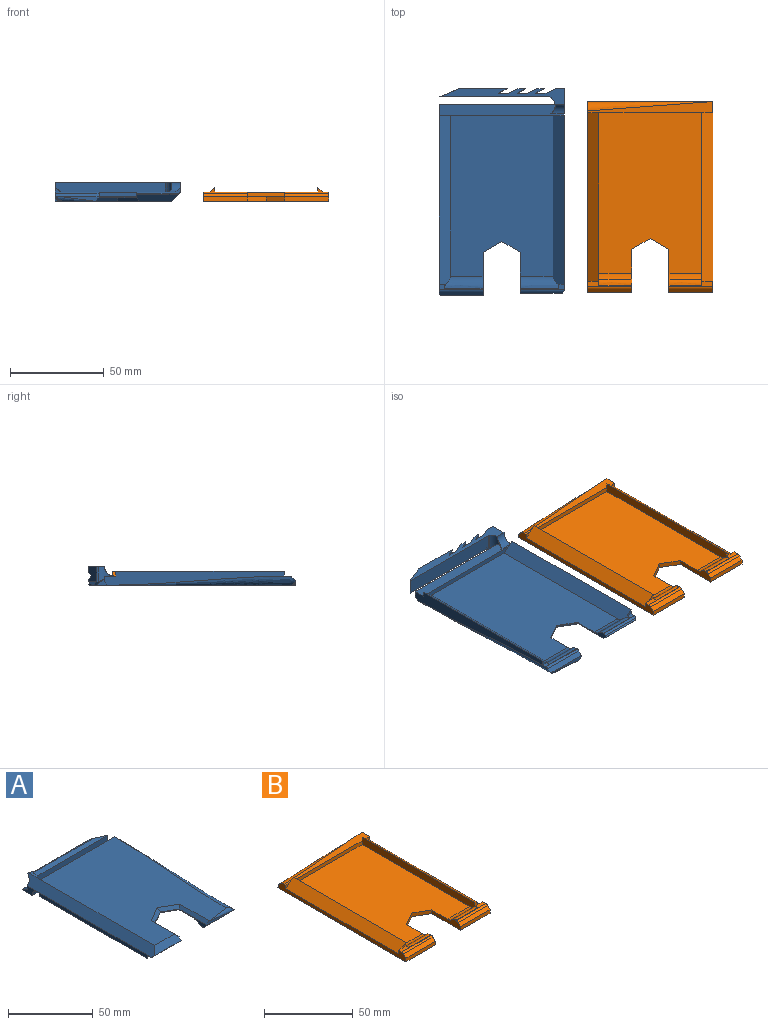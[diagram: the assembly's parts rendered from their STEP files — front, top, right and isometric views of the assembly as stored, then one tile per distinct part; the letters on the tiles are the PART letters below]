
ASSEMBLY  parts=2 mates=1
PART A: 78 faces, bbox 67x117.9x10 mm
  f0: plane 51.83x3.78mm, normal (0,0,1), area 23.2mm2, adj f12,f14,f16,f18,f20,f22,f24,f26
  f1: plane 90x2.5mm, normal (-1,0,0), area 225mm2, adj f41,f44,f48,f62
  f2: plane 3.72x1.44mm, normal (0,1,0), area 4.9mm2, adj f5,f13,f23,f51
  f3: plane 3.84x0.23mm, normal (0,1,0), area 0.4mm2, adj f5,f17,f51
  f4: plane 3.72x0.84mm, normal (0,1,0), area 2.7mm2, adj f5,f11,f19,f51
  f5: plane 67x8.5mm, normal (0,0,-1), area 257.4mm2, adj f2,f3,f4,f6,f7,f9,f11,f13
  f6: plane 13.46x5mm, normal (-1,0,0), area 31.5mm2, adj f5,f50,f51,f62,f75
  f7: plane 11x8mm, normal (0.38,0.93,0), area 87.2mm2, adj f5,f8,f9,f36,f50,f51,f52,f66
  f8: plane 22.52x1.36mm, normal (0,1,0), area 15.3mm2, adj f7,f52,f65
  f9: plane 25.45x3.36mm, normal (0,1,0), area 66mm2, adj f5,f7,f25,f51
  f10: plane 100x62mm, normal (0,0,1), area 5175.6mm2, adj f61,f62,f67,f70,f71,f72,f73,f76
  f11: plane 5.59x2.59mm, normal (0.4,0.92,0), area 10.5mm2, adj f4,f5,f15,f51
  f12: plane 4.04x2.59mm, normal (0.4,0.92,0), area 6.5mm2, adj f0,f16,f52,f69
  f13: plane 4.8x2.92mm, normal (-0.46,-0.89,0), area 11.2mm2, adj f2,f5,f15,f51
  f14: plane 3.89x2.92mm, normal (-0.46,-0.89,0), area 7.2mm2, adj f0,f16,f52,f68
  f15: plane 5.49x2.92mm, normal (0,1,0), area 15.1mm2, adj f5,f11,f13,f51
  f16: plane 5.49x2.92mm, normal (0,1,0), area 15.1mm2, adj f0,f12,f14,f52
  f17: plane 5.59x2.45mm, normal (0.4,0.92,0), area 6.8mm2, adj f3,f5,f21,f51
  f18: plane 5.21x2.29mm, normal (0.4,0.92,0), area 6.6mm2, adj f0,f22,f52,f62
  f19: plane 4.8x2.45mm, normal (-0.46,-0.89,0), area 7.9mm2, adj f4,f5,f21,f51
  f20: plane 3.2x2.32mm, normal (-0.46,-0.89,0), area 4.8mm2, adj f0,f22,f52,f69
  f21: plane 5.49x2.32mm, normal (0,1,0), area 11.8mm2, adj f5,f17,f19,f51
  f22: plane 5.49x2.32mm, normal (0,1,0), area 11.8mm2, adj f0,f18,f20,f52
  f23: plane 5.59x3.2mm, normal (0.4,0.92,0), area 14.2mm2, adj f2,f5,f27,f51
  f24: plane 4.85x3.2mm, normal (0.4,0.92,0), area 9.4mm2, adj f0,f28,f52,f68
  f25: plane 4.8x3.53mm, normal (-0.46,-0.89,0), area 14.4mm2, adj f5,f9,f27,f51
  f26: plane 4.59x3.53mm, normal (-0.46,-0.89,0), area 10mm2, adj f0,f28,f52,f65
  f27: plane 5.49x3.53mm, normal (0,1,0), area 18.5mm2, adj f5,f23,f25,f51
  f28: plane 5.49x3.53mm, normal (0,1,0), area 18.5mm2, adj f0,f24,f26,f52
  f29: plane 62x3mm, normal (0,1,0), area 186mm2, adj f35,f38,f45,f67,f74
  f30: plane 61x2.5mm, normal (0,-1,0), area 145mm2, adj f40,f41,f42,f45
  f31: plane 21.82x3mm, normal (1,0,0), area 23mm2, adj f32,f40,f49,f54,f56,f58,f59,f61
  f32: plane 10x5.77mm, normal (0.5,-0.87,0), area 5.8mm2, adj f31,f33,f40,f71
  f33: plane 10x5.77mm, normal (-0.5,-0.87,0), area 5.8mm2, adj f32,f34,f40,f73
  f34: plane 23.07x3mm, normal (-1,0,0), area 25.9mm2, adj f33,f37,f40,f46,f53,f55,f57,f60
  f35: plane 99.09x7.5mm, normal (1,0,0), area 474.7mm2, adj f29,f42,f43,f45,f46,f47,f67,f77
  f36: plane 59x8mm, normal (0,-1,0), area 472mm2, adj f5,f7,f39,f64
  f37: plane 19.92x2.5mm, normal (0,-1,0), area 25.4mm2, adj f34,f57,f72,f76
  f38: plane 6.4x3.66mm, normal (1,0,0), area 10.1mm2, adj f29,f62,f63,f67
  f39: plane 8x0.82mm, normal (0.55,-0.83,0), area 7.9mm2, adj f5,f36,f63,f74
  f40: plane 85.67x55mm, normal (0,0,-1), area 4399.3mm2, adj f30,f31,f32,f33,f34,f41,f42,f53
  f41: plane 92.28x6mm, normal (0.64,0,-0.77), area 698.9mm2, adj f1,f30,f40,f44,f48,f49,f54,f56
  f42: plane 92.28x6mm, normal (-0.64,0,-0.77), area 698.9mm2, adj f30,f35,f40,f43,f46,f47,f53,f55
  f43: plane 3x2.5mm, normal (0,1,0), area 3.7mm2, adj f35,f42,f45
  f44: plane 3x2.5mm, normal (0,1,0), area 3.7mm2, adj f1,f41,f45
  f45: plane 67x6mm, normal (0,0,-1), area 374.2mm2, adj f29,f30,f35,f43,f44,f62,f74,f75
  f46: plane 23.5x2.67mm, normal (0,0,-1), area 16mm2, adj f34,f35,f42,f47,f55,f60
  f47: plane 3x2.5mm, normal (0,-1,0), area 3.7mm2, adj f35,f42,f46
  f48: plane 3x2.5mm, normal (0,-1,0), area 3.8mm2, adj f1,f41,f49
  f49: plane 23.5x2.67mm, normal (0,0,-1), area 16mm2, adj f31,f41,f48,f56,f59,f62
  f50: plane 59.07x4.95mm, normal (-0.05,1,0), area 188.5mm2, adj f6,f7,f51,f52,f62
  f51: plane 59.07x4.35mm, normal (-0.05,0.5,0.86), area 139.3mm2, adj f2,f3,f4,f5,f6,f7,f9,f11
  f52: plane 56.63x4.23mm, normal (-0.05,0.5,-0.86), area 116.4mm2, adj f7,f8,f12,f14,f16,f18,f20,f22
  f53: cylinder r=5mm len=19mm, axis (-1,0,0), area 65.1mm2, adj f34,f40,f42,f55
  f54: cylinder r=5mm len=19mm, axis (-1,0,0), area 65.1mm2, adj f31,f40,f41,f56
  f55: bspline ~22.55x3.31mm, area 72.4mm2, adj f34,f42,f46,f53
  f56: bspline ~22.55x3.31mm, area 72.4mm2, adj f31,f41,f49,f54
  f57: plane 23.51x1.96mm, normal (0,-0.71,-0.71), area 62.8mm2, adj f34,f37,f60,f76,f77
  f58: plane 22.91x0.66mm, normal (0,-0.71,-0.71), area 21.2mm2, adj f31,f59,f61,f62
  f59: cylinder r=2mm len=23.5mm, axis (1,0,0), area 36.6mm2, adj f31,f49,f58,f62
  f60: cylinder r=2mm len=23.5mm, axis (1,0,0), area 36.9mm2, adj f34,f46,f57,f77
  f61: plane 22.25x3.75mm, normal (0,-0.71,0.71), area 105.2mm2, adj f10,f31,f58,f62,f70
  f62: plane 109.09x5mm, normal (-0.71,0,0.71), area 739.6mm2, adj f0,f1,f6,f10,f18,f38,f45,f49
  f63: plane 6x3.66mm, normal (0.39,-0.59,0.71), area 10.6mm2, adj f0,f38,f39,f64,f74
  f64: plane 59.61x2mm, normal (0,-0.71,0.71), area 153.3mm2, adj f0,f36,f63,f66
  f65: plane 25.24x2mm, normal (0,0.71,0.71), area 65.7mm2, adj f0,f8,f26,f52,f66
  f66: plane 11.39x4.5mm, normal (0.27,0.65,0.71), area 18.7mm2, adj f0,f7,f64,f65
  f67: plane 62x2mm, normal (0,0.71,0.71), area 175.4mm2, adj f10,f29,f35,f38
  f68: plane 7.37x1.68mm, normal (0,0.71,0.71), area 9.3mm2, adj f0,f14,f24,f52
  f69: plane 6.68x1.32mm, normal (0,0.71,0.71), area 7.4mm2, adj f0,f12,f20,f52
  f70: plane 21.23x2mm, normal (0.71,0,0.71), area 55.6mm2, adj f10,f31,f61,f71
  f71: plane 12x8.08mm, normal (0.35,-0.61,0.71), area 35.9mm2, adj f10,f32,f70,f73
  f72: plane 24.23x2mm, normal (-0.71,0,0.71), area 66.9mm2, adj f10,f34,f37,f73
  f73: plane 12x8.08mm, normal (-0.35,-0.61,0.71), area 35.9mm2, adj f10,f33,f71,f72
  f74: cylinder r=5mm len=8.45mm, axis (0,0,1), area 36.7mm2, adj f5,f29,f39,f45,f63,f75
  f75: cylinder r=5mm len=7.38mm, axis (-1,0,0), area 42.1mm2, adj f5,f6,f45,f74
  f76: bspline ~21.5x3mm, area 39.4mm2, adj f10,f37,f57,f77
  f77: bspline ~107.4x5mm, area 397.4mm2, adj f10,f35,f57,f60,f76
PART B: 36 faces, bbox 73.7x102x8 mm
  f0: plane 67x6mm, normal (0,0,1), area 234.5mm2, adj f1,f2,f3,f5,f20,f25,f26,f35
  f1: plane 102x5mm, normal (1,0,0), area 281.8mm2, adj f0,f11,f12,f13,f15,f18,f20,f21
  f2: plane 3x2.5mm, normal (0,-1,0), area 3.7mm2, adj f0,f5,f19
  f3: plane 55x2.5mm, normal (0,-1,0), area 137.5mm2, adj f0,f14,f16,f17
  f4: plane 3x2.5mm, normal (0,1,0), area 3.8mm2, adj f5,f19,f24
  f5: plane 102x5mm, normal (-1,0,0), area 276.4mm2, adj f0,f2,f4,f6,f13,f19,f24,f32
  f6: plane 23.5x2.5mm, normal (0,-1,0), area 58.7mm2, adj f5,f7,f13,f32
  f7: plane 23.07x5mm, normal (1,0,0), area 72mm2, adj f6,f8,f13,f14,f24,f28,f30,f32
  f8: plane 10x5.77mm, normal (0.5,-0.87,0), area 28.9mm2, adj f7,f9,f13,f14
  f9: plane 10x5.77mm, normal (-0.5,-0.87,0), area 28.9mm2, adj f8,f10,f13,f14
  f10: plane 23.07x5mm, normal (-1,0,0), area 72mm2, adj f9,f11,f13,f14,f21,f27,f29,f31
  f11: plane 23.5x2.5mm, normal (0,-1,0), area 58.7mm2, adj f1,f10,f13,f31
  f12: plane 67x5mm, normal (0,1,0), area 167.5mm2, adj f1,f13,f35
  f13: plane 102x67mm, normal (0,0,-1), area 6314.8mm2, adj f1,f5,f6,f7,f8,f9,f10,f11
  f14: plane 85.67x55mm, normal (0,0,1), area 4399.3mm2, adj f3,f7,f8,f9,f10,f16,f17,f27
  f15: plane 3x2.5mm, normal (0,1,0), area 3.7mm2, adj f1,f18,f21
  f16: plane 92.28x5mm, normal (1,0,0), area 447.4mm2, adj f3,f14,f19,f23,f24,f26,f28,f30
  f17: plane 92.28x5mm, normal (-1,0,0), area 447.4mm2, adj f3,f14,f18,f21,f22,f25,f27,f29
  f18: plane 90x6mm, normal (0.64,0,0.77), area 702.9mm2, adj f1,f15,f17,f20,f22,f25
  f19: plane 90x6mm, normal (-0.64,0,0.77), area 702.9mm2, adj f2,f4,f5,f16,f23,f26
  f20: plane 3x2.5mm, normal (0,-1,0), area 3.7mm2, adj f0,f1,f18
  f21: plane 23.5x2.67mm, normal (0,0,1), area 22.8mm2, adj f1,f10,f15,f17,f22,f29,f34
  f22: plane 3x2.5mm, normal (0,-1,0), area 3.8mm2, adj f17,f18,f21
  f23: plane 3x2.5mm, normal (0,-1,0), area 3.7mm2, adj f16,f19,f24
  f24: plane 23.5x2.67mm, normal (0,0,1), area 22.8mm2, adj f4,f5,f7,f16,f23,f30,f33
  f25: plane 3x2.5mm, normal (0,1,0), area 3.8mm2, adj f0,f17,f18
  f26: plane 3x2.5mm, normal (0,1,0), area 3.8mm2, adj f0,f16,f19
  f27: cylinder r=5mm len=17.5mm, axis (1,0,0), area 63.2mm2, adj f10,f14,f17,f29
  f28: cylinder r=5mm len=17.5mm, axis (1,0,0), area 63.2mm2, adj f7,f14,f16,f30
  f29: bspline ~19.25x3.31mm, area 63.3mm2, adj f10,f17,f21,f27
  f30: bspline ~19.25x3.31mm, area 63.3mm2, adj f7,f16,f24,f28
  f31: plane 23.5x1.91mm, normal (0,-0.71,0.71), area 63.6mm2, adj f1,f10,f11,f34
  f32: plane 23.5x1.91mm, normal (0,-0.71,0.71), area 63.6mm2, adj f5,f6,f7,f33
  f33: cylinder r=2mm len=23.5mm, axis (-1,0,0), area 36.9mm2, adj f5,f7,f24,f32
  f34: cylinder r=2mm len=23.5mm, axis (-1,0,0), area 36.9mm2, adj f1,f10,f21,f31
  f35: bspline ~73.7x5.5mm, area 263.2mm2, adj f0,f5,f12
PLACE A rot(axis=(0,1,0),180deg) t=(-79.07,2.78,1.17)mm
PLACE B t=(0.24,4.33,1.17)mm fixed
MATE planar A.f0 <-> B.f13  axis (0,0,-1) through (-73.53,55.82,-3.83)mm
